# Revit family: NBS_Allermuir_DmstcChrs_Oran_Chair
name_source: partatom
category: Furniture
revit_build: Autodesk Revit 2016 (Build: 20161004_0715(x64)
units: mm (PartAtom-declared; Revit-internal decimal feet)

## family parameters
Always vertical = Yes
Cut with Voids When Loaded = No
Room Calculation Point = No
Shared = No
Work Plane-Based = No

## types (1)
- ORA100
    AssetType = Moveable
    BIMObjectName = NBS_Allermuir_DomesticChairs_Oran_ORA100
    Category = Pr_40_50_12_22:Dining chairs
    Chair = Yes
    Description = Arm chair
    DurationUnit = year
    ExpectedLife = 5
    Features = Fully upholstered, traditional carcass construction, tensioned seat support, feather wrapped sprung seat foam, cast aluminium legs and aluminium perimeter frame finished in black powder coat, curled feather filled cushion with fire retardant inner cover, plastic glides, aluminium frame available in tusk grey powder coat, wo-tone upholstery
    FrameDepth = 910 mm  [stored 2.98556 ft]
    FrameLength = 898 mm
    FrameMaterials = Aluminium
    FramesColour = Black, tusk grey
    FramesFinish = Powder coat
    HighestSeatingHeight = 440 mm  [stored 1.44357 ft]
    IfcExportAs = IfcFurnitureType
    IfcExportType = CHAIR
    IsBuiltIn = No
    LowestSeatingHeight = 440 mm  [stored 1.44357 ft]
    ManufacturerName = Allermuir
    ManufacturerURL = http://www.thesenatorgroup.com
    ModelNumber = ORA100
    ModelReference = Oran
    NBSCertification = www.nationalbimlibrary.com/cert/e5nbcsfr
    NBSDescription = Domestic chairs
    NBSReference = 45-35-20/365
    Name = DomesticChairs_Oran_ORA100_Allermuir
    NominalDepth = 947 mm  [stored 3.10696 ft]
    NominalHeight = 704 mm  [stored 2.30971 ft]
    NominalLength = 938 mm
    NominalWidth = 955 mm  [stored 3.1332 ft]
    SeatFrameMaterial = NBS_Concept
    SeatSeatingMaterial = NBS_Concept
    SeatingHeight = 440 mm  [stored 1.44357 ft]
    SeatsAndBacksFinish = Fully upholstered
    Size = 940 x 955 x 700 mm
    Status = UNSET
    Uniclass2015Code = Pr_40_50_12_22
    Uniclass2015Title = Dining chairs
    Uniclass2015Version = Products v1.9
    Version = 1
    WarrantyDescription = Allermuir warrant that its manufactured products are free from manufacturing defects in materials or workmanship for a period of five years
    WarrantyDurationParts = 5
    WarrantyDurationUnit = year

note: [stored X ft] marks values corroborated as IEEE doubles in the binary element streams (Revit-internal decimal feet)

## geometry (parser evidence)
native form markers: Sweep x14
no freeform markers — native parametric forms only
